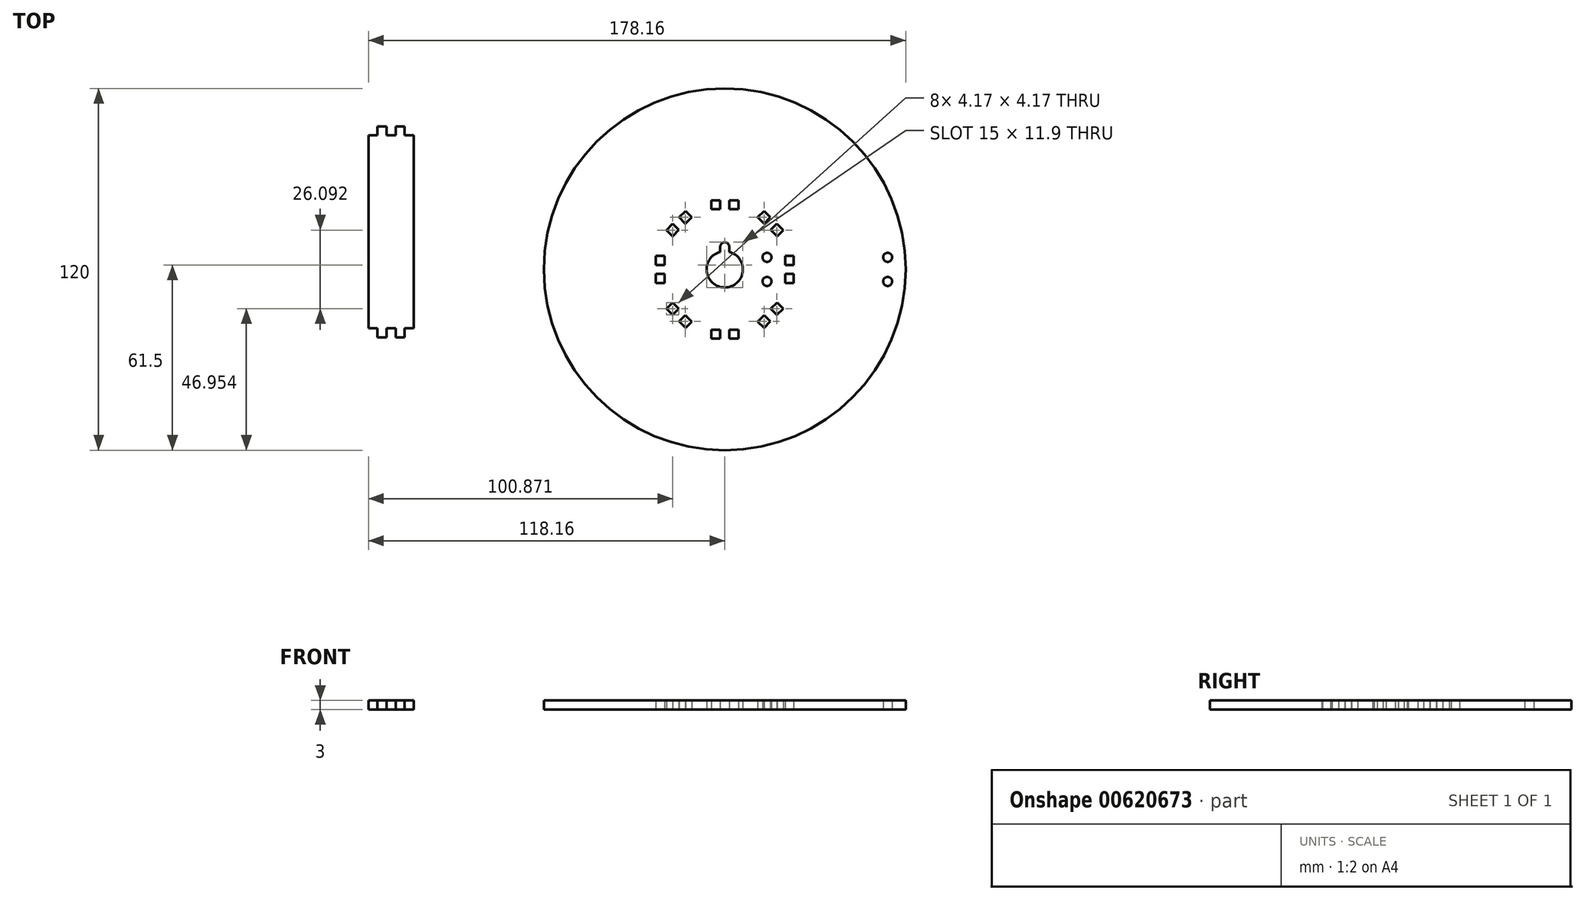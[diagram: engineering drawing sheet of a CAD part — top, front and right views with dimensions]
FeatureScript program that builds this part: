
annotation { "Feature Type Name" : "Feature", "Feature Type Description" : "" }
export const myFeature = defineFeature(function(context is Context, id is Id, definition is map)
    precondition{}
    {
        {
            var Q0;
            Q0=qCreatedBy(makeId("Top.planeOp"),FACE);
            var sketch = newSketch(context, id + "F0", { "sketchPlane" : qUnion([Q0])});
            skCircle(sketch, "E0", {"center": v(0, 0) * mm, "radius": 60 * mm});
            skArc(sketch, "E1", {"start": v(-1.5, 5.8) * mm, "mid": v(0, -6) * mm, "end": v(1.5, 5.8) * mm});
            skCircle(sketch, "E2", {"center": v(0, 0) * mm, "radius": 20 * mm});
            skLineSegment(sketch, "E3.bottom", {"start": v(-286.24, 2.98) * mm, "end": v(-283.34, 2.98) * mm});
            skLineSegment(sketch, "E3.top", {"start": v(-286.24, -0.02) * mm, "end": v(-283.34, -0.02) * mm});
            skLineSegment(sketch, "E3.left", {"start": v(-286.24, 2.98) * mm, "end": v(-286.24, -0.02) * mm});
            skLineSegment(sketch, "E3.right", {"start": v(-283.34, 2.98) * mm, "end": v(-283.34, -0.02) * mm});
            skLineSegment(sketch, "E4.bottom", {"start": v(-286.24, -3.02) * mm, "end": v(-283.34, -3.02) * mm});
            skLineSegment(sketch, "E4.top", {"start": v(-286.24, -6.02) * mm, "end": v(-283.34, -6.02) * mm});
            skLineSegment(sketch, "E4.left", {"start": v(-286.24, -3.02) * mm, "end": v(-286.24, -6.02) * mm});
            skLineSegment(sketch, "E4.right", {"start": v(-283.34, -3.02) * mm, "end": v(-283.34, -6.02) * mm});
            skLineSegment(sketch, "E5.bottom", {"start": v(-243.34, 2.98) * mm, "end": v(-240.44, 2.98) * mm});
            skLineSegment(sketch, "E5.top", {"start": v(-243.34, -0.02) * mm, "end": v(-240.44, -0.02) * mm});
            skLineSegment(sketch, "E5.left", {"start": v(-243.34, 2.98) * mm, "end": v(-243.34, -0.02) * mm});
            skLineSegment(sketch, "E5.right", {"start": v(-240.44, 2.98) * mm, "end": v(-240.44, -0.02) * mm});
            skLineSegment(sketch, "E6.bottom", {"start": v(-243.34, -3.02) * mm, "end": v(-240.44, -3.02) * mm});
            skLineSegment(sketch, "E6.top", {"start": v(-243.34, -6.02) * mm, "end": v(-240.44, -6.02) * mm});
            skLineSegment(sketch, "E6.left", {"start": v(-243.34, -3.02) * mm, "end": v(-243.34, -6.02) * mm});
            skLineSegment(sketch, "E6.right", {"start": v(-240.44, -3.02) * mm, "end": v(-240.44, -6.02) * mm});
            skLineSegment(sketch, "E7.bottom", {"start": v(-258.84, 21.38) * mm, "end": v(-258.84, 18.48) * mm});
            skLineSegment(sketch, "E7.top", {"start": v(-261.84, 21.38) * mm, "end": v(-261.84, 18.48) * mm});
            skLineSegment(sketch, "E7.left", {"start": v(-258.84, 21.38) * mm, "end": v(-261.84, 21.38) * mm});
            skLineSegment(sketch, "E7.right", {"start": v(-258.84, 18.48) * mm, "end": v(-261.84, 18.48) * mm});
            skLineSegment(sketch, "E8.bottom", {"start": v(-264.84, 21.38) * mm, "end": v(-264.84, 18.48) * mm});
            skLineSegment(sketch, "E8.top", {"start": v(-267.84, 21.38) * mm, "end": v(-267.84, 18.48) * mm});
            skLineSegment(sketch, "E8.left", {"start": v(-264.84, 21.38) * mm, "end": v(-267.84, 21.38) * mm});
            skLineSegment(sketch, "E8.right", {"start": v(-264.84, 18.48) * mm, "end": v(-267.84, 18.48) * mm});
            skLineSegment(sketch, "E9.bottom", {"start": v(-258.84, -21.52) * mm, "end": v(-258.84, -24.42) * mm});
            skLineSegment(sketch, "E9.top", {"start": v(-261.84, -21.52) * mm, "end": v(-261.84, -24.42) * mm});
            skLineSegment(sketch, "E9.left", {"start": v(-258.84, -21.52) * mm, "end": v(-261.84, -21.52) * mm});
            skLineSegment(sketch, "E9.right", {"start": v(-258.84, -24.42) * mm, "end": v(-261.84, -24.42) * mm});
            skLineSegment(sketch, "E10.bottom", {"start": v(-264.84, -21.52) * mm, "end": v(-264.84, -24.42) * mm});
            skLineSegment(sketch, "E10.top", {"start": v(-267.84, -21.52) * mm, "end": v(-267.84, -24.42) * mm});
            skLineSegment(sketch, "E10.left", {"start": v(-264.84, -21.52) * mm, "end": v(-267.84, -21.52) * mm});
            skLineSegment(sketch, "E10.right", {"start": v(-264.84, -24.42) * mm, "end": v(-267.84, -24.42) * mm});
            skPoint(sketch, "E11", {"position": v(-263.34, 18.48) * mm});
            skPoint(sketch, "E12", {"position": v(-263.34, -21.52) * mm});
            skPoint(sketch, "E13", {"position": v(-283.34, -1.52) * mm});
            skPoint(sketch, "E14", {"position": v(-243.34, -1.52) * mm});
            skPoint(sketch, "E15", {"position": v(-263.34, -1.52) * mm});
            skLineSegment(sketch, "E16.bottom", {"start": v(-282.72, -14.53) * mm, "end": v(-280.67, -12.48) * mm});
            skLineSegment(sketch, "E16.top", {"start": v(-280.6, -16.65) * mm, "end": v(-278.54, -14.6) * mm});
            skLineSegment(sketch, "E16.left", {"start": v(-282.72, -14.53) * mm, "end": v(-280.6, -16.65) * mm});
            skLineSegment(sketch, "E16.right", {"start": v(-280.67, -12.48) * mm, "end": v(-278.54, -14.6) * mm});
            skLineSegment(sketch, "E17.bottom", {"start": v(-278.47, -18.77) * mm, "end": v(-276.42, -16.72) * mm});
            skLineSegment(sketch, "E17.top", {"start": v(-276.35, -20.9) * mm, "end": v(-274.3, -18.84) * mm});
            skLineSegment(sketch, "E17.left", {"start": v(-278.47, -18.77) * mm, "end": v(-276.35, -20.9) * mm});
            skLineSegment(sketch, "E17.right", {"start": v(-276.42, -16.72) * mm, "end": v(-274.3, -18.84) * mm});
            skLineSegment(sketch, "E18.bottom", {"start": v(-252.38, 15.8) * mm, "end": v(-250.33, 17.85) * mm});
            skLineSegment(sketch, "E18.top", {"start": v(-250.26, 13.68) * mm, "end": v(-248.2, 15.73) * mm});
            skLineSegment(sketch, "E18.left", {"start": v(-252.38, 15.8) * mm, "end": v(-250.26, 13.68) * mm});
            skLineSegment(sketch, "E18.right", {"start": v(-250.33, 17.85) * mm, "end": v(-248.2, 15.73) * mm});
            skLineSegment(sketch, "E19.bottom", {"start": v(-248.14, 11.56) * mm, "end": v(-246.09, 13.61) * mm});
            skLineSegment(sketch, "E19.top", {"start": v(-246.02, 9.44) * mm, "end": v(-243.97, 11.5) * mm});
            skLineSegment(sketch, "E19.left", {"start": v(-248.14, 11.56) * mm, "end": v(-246.02, 9.44) * mm});
            skLineSegment(sketch, "E19.right", {"start": v(-246.09, 13.61) * mm, "end": v(-243.97, 11.5) * mm});
            skLineSegment(sketch, "E20.bottom", {"start": v(-276.35, 17.85) * mm, "end": v(-274.3, 15.8) * mm});
            skLineSegment(sketch, "E20.top", {"start": v(-278.47, 15.73) * mm, "end": v(-276.42, 13.68) * mm});
            skLineSegment(sketch, "E20.left", {"start": v(-276.35, 17.85) * mm, "end": v(-278.47, 15.73) * mm});
            skLineSegment(sketch, "E20.right", {"start": v(-274.3, 15.8) * mm, "end": v(-276.42, 13.68) * mm});
            skLineSegment(sketch, "E21.bottom", {"start": v(-280.6, 13.61) * mm, "end": v(-278.54, 11.56) * mm});
            skLineSegment(sketch, "E21.top", {"start": v(-282.72, 11.5) * mm, "end": v(-280.67, 9.44) * mm});
            skLineSegment(sketch, "E21.left", {"start": v(-280.6, 13.61) * mm, "end": v(-282.72, 11.5) * mm});
            skLineSegment(sketch, "E21.right", {"start": v(-278.54, 11.56) * mm, "end": v(-280.67, 9.44) * mm});
            skLineSegment(sketch, "E22.bottom", {"start": v(-246.02, -12.48) * mm, "end": v(-243.97, -14.53) * mm});
            skLineSegment(sketch, "E22.top", {"start": v(-248.14, -14.6) * mm, "end": v(-246.09, -16.65) * mm});
            skLineSegment(sketch, "E22.left", {"start": v(-246.02, -12.48) * mm, "end": v(-248.14, -14.6) * mm});
            skLineSegment(sketch, "E22.right", {"start": v(-243.97, -14.53) * mm, "end": v(-246.09, -16.65) * mm});
            skLineSegment(sketch, "E23.bottom", {"start": v(-250.26, -16.72) * mm, "end": v(-248.2, -18.77) * mm});
            skLineSegment(sketch, "E23.top", {"start": v(-252.38, -18.84) * mm, "end": v(-250.33, -20.9) * mm});
            skLineSegment(sketch, "E23.left", {"start": v(-250.26, -16.72) * mm, "end": v(-252.38, -18.84) * mm});
            skLineSegment(sketch, "E23.right", {"start": v(-248.2, -18.77) * mm, "end": v(-250.33, -20.9) * mm});
            skPoint(sketch, "E24", {"position": v(-277.48, 12.62) * mm});
            skPoint(sketch, "E25", {"position": v(-249.2, -15.66) * mm});
            skPoint(sketch, "E26", {"position": v(-277.48, -15.66) * mm});
            skPoint(sketch, "E27", {"position": v(-249.2, 12.62) * mm});
            skLineSegment(sketch, "E28.0", {"start": v(-277.48, 12.62) * mm, "end": v(-276.42, 13.68) * mm, "construction": true});
            skLineSegment(sketch, "E28.1", {"start": v(-277.48, 12.62) * mm, "end": v(-277.48, 12.62) * mm});
            skLineSegment(sketch, "E28.8", {"start": v(-277.48, -15.66) * mm, "end": v(-277.48, -15.66) * mm});
            skLineSegment(sketch, "E28.9", {"start": v(-277.48, -15.66) * mm, "end": v(-278.54, -14.6) * mm, "construction": true});
            skLineSegment(sketch, "E28.16", {"start": v(-248.14, 11.56) * mm, "end": v(-248.14, 11.56) * mm});
            skLineSegment(sketch, "E28.17", {"start": v(-248.14, 11.56) * mm, "end": v(-249.2, 12.62) * mm, "construction": true});
            skLineSegment(sketch, "E28.24", {"start": v(-249.2, -15.66) * mm, "end": v(-248.14, -14.6) * mm, "construction": true});
            skLineSegment(sketch, "E28.25", {"start": v(-249.2, -15.66) * mm, "end": v(-249.2, -15.66) * mm});
            skLineSegment(sketch, "E28.32", {"start": v(-249.2, -15.66) * mm, "end": v(-235.06, -1.52) * mm, "construction": true});
            skLineSegment(sketch, "E28.33", {"start": v(-235.06, -1.52) * mm, "end": v(-249.2, 12.62) * mm, "construction": true});
            skLineSegment(sketch, "E28.40", {"start": v(-263.34, -1.52) * mm, "end": v(-249.2, 12.62) * mm, "construction": true});
            skLineSegment(sketch, "E28.41", {"start": v(-263.34, -1.52) * mm, "end": v(-277.48, 12.62) * mm, "construction": true});
            skLineSegment(sketch, "E29.0", {"start": v(-278.54, 11.56) * mm, "end": v(-276.42, 13.68) * mm, "construction": true});
            skLineSegment(sketch, "E30.0", {"start": v(-248.2, -18.77) * mm, "end": v(-246.09, -16.65) * mm, "construction": true});
            skLineSegment(sketch, "E31.0", {"start": v(-280.67, -12.48) * mm, "end": v(-252.38, 15.8) * mm, "construction": true});
            skLineSegment(sketch, "E32.0", {"start": v(-249.2, 12.62) * mm, "end": v(-250.26, 13.68) * mm, "construction": true});
            skLineSegment(sketch, "E33.0", {"start": v(-246.09, 13.61) * mm, "end": v(-248.2, 15.73) * mm, "construction": true});
            skLineSegment(sketch, "E34.0", {"start": v(-276.42, -16.72) * mm, "end": v(-278.54, -14.6) * mm, "construction": true});
            skLineSegment(sketch, "E35.0", {"start": v(-246.02, -12.48) * mm, "end": v(-274.3, 15.8) * mm, "construction": true});
            skLineSegment(sketch, "E36.bottom", {"start": v(-22.9, 4.5) * mm, "end": v(-20, 4.5) * mm});
            skLineSegment(sketch, "E36.top", {"start": v(-22.9, 1.5) * mm, "end": v(-20, 1.5) * mm});
            skLineSegment(sketch, "E36.left", {"start": v(-22.9, 4.5) * mm, "end": v(-22.9, 1.5) * mm});
            skLineSegment(sketch, "E36.right", {"start": v(-20, 4.5) * mm, "end": v(-20, 1.5) * mm});
            skLineSegment(sketch, "E37.bottom", {"start": v(-22.9, -1.5) * mm, "end": v(-20, -1.5) * mm});
            skLineSegment(sketch, "E37.top", {"start": v(-22.9, -4.5) * mm, "end": v(-20, -4.5) * mm});
            skLineSegment(sketch, "E37.left", {"start": v(-22.9, -1.5) * mm, "end": v(-22.9, -4.5) * mm});
            skLineSegment(sketch, "E37.right", {"start": v(-20, -1.5) * mm, "end": v(-20, -4.5) * mm});
            skLineSegment(sketch, "E38.bottom", {"start": v(20, 4.5) * mm, "end": v(22.9, 4.5) * mm});
            skLineSegment(sketch, "E38.top", {"start": v(20, 1.5) * mm, "end": v(22.9, 1.5) * mm});
            skLineSegment(sketch, "E38.left", {"start": v(20, 4.5) * mm, "end": v(20, 1.5) * mm});
            skLineSegment(sketch, "E38.right", {"start": v(22.9, 4.5) * mm, "end": v(22.9, 1.5) * mm});
            skLineSegment(sketch, "E39.bottom", {"start": v(20, -1.5) * mm, "end": v(22.9, -1.5) * mm});
            skLineSegment(sketch, "E39.top", {"start": v(20, -4.5) * mm, "end": v(22.9, -4.5) * mm});
            skLineSegment(sketch, "E39.left", {"start": v(20, -1.5) * mm, "end": v(20, -4.5) * mm});
            skLineSegment(sketch, "E39.right", {"start": v(22.9, -1.5) * mm, "end": v(22.9, -4.5) * mm});
            skLineSegment(sketch, "E40.bottom", {"start": v(4.5, 22.9) * mm, "end": v(4.5, 20) * mm});
            skLineSegment(sketch, "E40.top", {"start": v(1.5, 22.9) * mm, "end": v(1.5, 20) * mm});
            skLineSegment(sketch, "E40.left", {"start": v(4.5, 22.9) * mm, "end": v(1.5, 22.9) * mm});
            skLineSegment(sketch, "E40.right", {"start": v(4.5, 20) * mm, "end": v(1.5, 20) * mm});
            skLineSegment(sketch, "E41.bottom", {"start": v(-1.5, 22.9) * mm, "end": v(-1.5, 20) * mm});
            skLineSegment(sketch, "E41.top", {"start": v(-4.5, 22.9) * mm, "end": v(-4.5, 20) * mm});
            skLineSegment(sketch, "E41.left", {"start": v(-1.5, 22.9) * mm, "end": v(-4.5, 22.9) * mm});
            skLineSegment(sketch, "E41.right", {"start": v(-1.5, 20) * mm, "end": v(-4.5, 20) * mm});
            skLineSegment(sketch, "E42.bottom", {"start": v(4.5, -20) * mm, "end": v(4.5, -22.9) * mm});
            skLineSegment(sketch, "E42.top", {"start": v(1.5, -20) * mm, "end": v(1.5, -22.9) * mm});
            skLineSegment(sketch, "E42.left", {"start": v(4.5, -20) * mm, "end": v(1.5, -20) * mm});
            skLineSegment(sketch, "E42.right", {"start": v(4.5, -22.9) * mm, "end": v(1.5, -22.9) * mm});
            skLineSegment(sketch, "E43.bottom", {"start": v(-1.5, -20) * mm, "end": v(-1.5, -22.9) * mm});
            skLineSegment(sketch, "E43.top", {"start": v(-4.5, -20) * mm, "end": v(-4.5, -22.9) * mm});
            skLineSegment(sketch, "E43.left", {"start": v(-1.5, -20) * mm, "end": v(-4.5, -20) * mm});
            skLineSegment(sketch, "E43.right", {"start": v(-1.5, -22.9) * mm, "end": v(-4.5, -22.9) * mm});
            skPoint(sketch, "E44", {"position": v(0, 20) * mm});
            skPoint(sketch, "E45", {"position": v(0, -20) * mm});
            skPoint(sketch, "E46", {"position": v(-20, 0) * mm});
            skPoint(sketch, "E47", {"position": v(20, 0) * mm});
            skLineSegment(sketch, "E48.bottom", {"start": v(-19.37, -13.01) * mm, "end": v(-17.32, -10.96) * mm});
            skLineSegment(sketch, "E48.top", {"start": v(-17.25, -15.13) * mm, "end": v(-15.2, -13.08) * mm});
            skLineSegment(sketch, "E48.left", {"start": v(-19.37, -13.01) * mm, "end": v(-17.25, -15.13) * mm});
            skLineSegment(sketch, "E48.right", {"start": v(-17.32, -10.96) * mm, "end": v(-15.2, -13.08) * mm});
            skLineSegment(sketch, "E49.bottom", {"start": v(-15.13, -17.25) * mm, "end": v(-13.08, -15.2) * mm});
            skLineSegment(sketch, "E49.top", {"start": v(-13.01, -19.37) * mm, "end": v(-10.96, -17.32) * mm});
            skLineSegment(sketch, "E49.left", {"start": v(-15.13, -17.25) * mm, "end": v(-13.01, -19.37) * mm});
            skLineSegment(sketch, "E49.right", {"start": v(-13.08, -15.2) * mm, "end": v(-10.96, -17.32) * mm});
            skLineSegment(sketch, "E50.bottom", {"start": v(10.96, 17.32) * mm, "end": v(13.01, 19.37) * mm});
            skLineSegment(sketch, "E50.top", {"start": v(13.08, 15.2) * mm, "end": v(15.13, 17.25) * mm});
            skLineSegment(sketch, "E50.left", {"start": v(10.96, 17.32) * mm, "end": v(13.08, 15.2) * mm});
            skLineSegment(sketch, "E50.right", {"start": v(13.01, 19.37) * mm, "end": v(15.13, 17.25) * mm});
            skLineSegment(sketch, "E51.bottom", {"start": v(15.2, 13.08) * mm, "end": v(17.25, 15.13) * mm});
            skLineSegment(sketch, "E51.top", {"start": v(17.32, 10.96) * mm, "end": v(19.37, 13.01) * mm});
            skLineSegment(sketch, "E51.left", {"start": v(15.2, 13.08) * mm, "end": v(17.32, 10.96) * mm});
            skLineSegment(sketch, "E51.right", {"start": v(17.25, 15.13) * mm, "end": v(19.37, 13.01) * mm});
            skLineSegment(sketch, "E52.bottom", {"start": v(-13.01, 19.37) * mm, "end": v(-10.96, 17.32) * mm});
            skLineSegment(sketch, "E52.top", {"start": v(-15.13, 17.25) * mm, "end": v(-13.08, 15.2) * mm});
            skLineSegment(sketch, "E52.left", {"start": v(-13.01, 19.37) * mm, "end": v(-15.13, 17.25) * mm});
            skLineSegment(sketch, "E52.right", {"start": v(-10.96, 17.32) * mm, "end": v(-13.08, 15.2) * mm});
            skLineSegment(sketch, "E53.bottom", {"start": v(-17.25, 15.13) * mm, "end": v(-15.2, 13.08) * mm});
            skLineSegment(sketch, "E53.top", {"start": v(-19.37, 13.01) * mm, "end": v(-17.32, 10.96) * mm});
            skLineSegment(sketch, "E53.left", {"start": v(-17.25, 15.13) * mm, "end": v(-19.37, 13.01) * mm});
            skLineSegment(sketch, "E53.right", {"start": v(-15.2, 13.08) * mm, "end": v(-17.32, 10.96) * mm});
            skLineSegment(sketch, "E54.bottom", {"start": v(17.32, -10.96) * mm, "end": v(19.37, -13.01) * mm});
            skLineSegment(sketch, "E54.top", {"start": v(15.2, -13.08) * mm, "end": v(17.25, -15.13) * mm});
            skLineSegment(sketch, "E54.left", {"start": v(17.32, -10.96) * mm, "end": v(15.2, -13.08) * mm});
            skLineSegment(sketch, "E54.right", {"start": v(19.37, -13.01) * mm, "end": v(17.25, -15.13) * mm});
            skLineSegment(sketch, "E55.bottom", {"start": v(13.08, -15.2) * mm, "end": v(15.13, -17.25) * mm});
            skLineSegment(sketch, "E55.top", {"start": v(10.96, -17.32) * mm, "end": v(13.01, -19.37) * mm});
            skLineSegment(sketch, "E55.left", {"start": v(13.08, -15.2) * mm, "end": v(10.96, -17.32) * mm});
            skLineSegment(sketch, "E55.right", {"start": v(15.13, -17.25) * mm, "end": v(13.01, -19.37) * mm});
            skPoint(sketch, "E56", {"position": v(-14.14, 14.14) * mm});
            skPoint(sketch, "E57", {"position": v(14.14, -14.14) * mm});
            skPoint(sketch, "E58", {"position": v(-14.14, -14.14) * mm});
            skPoint(sketch, "E59", {"position": v(14.14, 14.14) * mm});
            skLineSegment(sketch, "E60.0", {"start": v(-14.14, 14.14) * mm, "end": v(-13.08, 15.2) * mm, "construction": true});
            skLineSegment(sketch, "E60.1", {"start": v(-14.14, 14.14) * mm, "end": v(-14.14, 14.14) * mm});
            skLineSegment(sketch, "E60.8", {"start": v(-14.14, -14.14) * mm, "end": v(-14.14, -14.14) * mm});
            skLineSegment(sketch, "E60.9", {"start": v(-14.14, -14.14) * mm, "end": v(-15.2, -13.08) * mm, "construction": true});
            skLineSegment(sketch, "E60.16", {"start": v(15.2, 13.08) * mm, "end": v(15.2, 13.08) * mm});
            skLineSegment(sketch, "E60.17", {"start": v(15.2, 13.08) * mm, "end": v(14.14, 14.14) * mm, "construction": true});
            skLineSegment(sketch, "E60.24", {"start": v(14.14, -14.14) * mm, "end": v(15.2, -13.08) * mm, "construction": true});
            skLineSegment(sketch, "E60.25", {"start": v(14.14, -14.14) * mm, "end": v(14.14, -14.14) * mm});
            skLineSegment(sketch, "E60.32", {"start": v(14.14, -14.14) * mm, "end": v(28.28, 0) * mm, "construction": true});
            skLineSegment(sketch, "E60.33", {"start": v(28.28, 0) * mm, "end": v(14.14, 14.14) * mm, "construction": true});
            skLineSegment(sketch, "E60.40", {"start": v(0, 0) * mm, "end": v(14.14, 14.14) * mm, "construction": true});
            skLineSegment(sketch, "E60.41", {"start": v(0, 0) * mm, "end": v(-14.14, 14.14) * mm, "construction": true});
            skLineSegment(sketch, "E61.0", {"start": v(-15.2, 13.08) * mm, "end": v(-13.08, 15.2) * mm, "construction": true});
            skLineSegment(sketch, "E62.0", {"start": v(15.13, -17.25) * mm, "end": v(17.25, -15.13) * mm, "construction": true});
            skLineSegment(sketch, "E63.0", {"start": v(-17.32, -10.96) * mm, "end": v(10.96, 17.32) * mm, "construction": true});
            skLineSegment(sketch, "E64.0", {"start": v(14.14, 14.14) * mm, "end": v(13.08, 15.2) * mm, "construction": true});
            skLineSegment(sketch, "E65.0", {"start": v(17.25, 15.13) * mm, "end": v(15.13, 17.25) * mm, "construction": true});
            skLineSegment(sketch, "E66.0", {"start": v(-13.08, -15.2) * mm, "end": v(-15.2, -13.08) * mm, "construction": true});
            skLineSegment(sketch, "E67.0", {"start": v(17.32, -10.96) * mm, "end": v(-10.96, 17.32) * mm, "construction": true});
            skCircle(sketch, "E68", {"center": v(54, 4) * mm, "radius": 1.5 * mm});
            skCircle(sketch, "E69", {"center": v(54, -4) * mm, "radius": 1.5 * mm});
            skCircle(sketch, "E70", {"center": v(14, 4) * mm, "radius": 1.5 * mm});
            skCircle(sketch, "E71", {"center": v(14, -4) * mm, "radius": 1.5 * mm});
            skLineSegment(sketch, "E72.bottom", {"start": v(0, 9) * mm, "end": v(0, 9) * mm});
            skLineSegment(sketch, "E72.top", {"start": v(-1.5, 0) * mm, "end": v(1.5, 0) * mm});
            skLineSegment(sketch, "E72.left", {"start": v(-1.5, 7.5) * mm, "end": v(-1.5, 5.8) * mm});
            skLineSegment(sketch, "E72.right", {"start": v(1.5, 7.5) * mm, "end": v(1.5, 5.8) * mm});
            skPoint(sketch, "E73.visualSharp", {"position": v(-1.5, 9) * mm});
            skArc(sketch, "E73.filletArc", {"start": v(0, 9) * mm, "mid": v(-1.06, 8.56) * mm, "end": v(-1.5, 7.5) * mm});
            skPoint(sketch, "E74.visualSharp", {"position": v(1.5, 9) * mm});
            skArc(sketch, "E74.filletArc", {"start": v(1.5, 7.5) * mm, "mid": v(1.06, 8.56) * mm, "end": v(0, 9) * mm});
            skLineSegment(sketch, "E75.trimOffspring", {"start": v(-1.5, 4.86) * mm, "end": v(-1.5, 0) * mm});
            skLineSegment(sketch, "E76.trimOffspring", {"start": v(1.5, 4.86) * mm, "end": v(1.5, 0) * mm});
            skSolve(sketch);
        }
        {
            var Q0;
            Q0=qCreatedBy(makeId("Top.planeOp"),FACE);
            var sketch = newSketch(context, id + "F1", { "sketchPlane" : qUnion([Q0])});
            skLineSegment(sketch, "E77.bottom", {"start": v(-115.16, 47.44) * mm, "end": v(-112.16, 47.44) * mm});
            skLineSegment(sketch, "E77.top", {"start": v(-115.16, -22.56) * mm, "end": v(-112.16, -22.56) * mm});
            skLineSegment(sketch, "E77.left", {"start": v(-115.16, 47.44) * mm, "end": v(-115.16, 44.44) * mm});
            skLineSegment(sketch, "E77.right", {"start": v(-106.16, 47.44) * mm, "end": v(-106.16, 44.44) * mm});
            skLineSegment(sketch, "E78.top", {"start": v(-112.16, 44.44) * mm, "end": v(-109.16, 44.44) * mm});
            skLineSegment(sketch, "E78.left", {"start": v(-112.16, 47.44) * mm, "end": v(-112.16, 44.44) * mm});
            skLineSegment(sketch, "E78.right", {"start": v(-109.16, 47.44) * mm, "end": v(-109.16, 44.44) * mm});
            skLineSegment(sketch, "E79.bottom", {"start": v(-112.16, -19.56) * mm, "end": v(-109.16, -19.56) * mm});
            skLineSegment(sketch, "E79.left", {"start": v(-112.16, -19.56) * mm, "end": v(-112.16, -22.56) * mm});
            skLineSegment(sketch, "E79.right", {"start": v(-109.16, -19.56) * mm, "end": v(-109.16, -22.56) * mm});
            skLineSegment(sketch, "E80.trimOffspring", {"start": v(-109.16, 47.44) * mm, "end": v(-106.16, 47.44) * mm});
            skLineSegment(sketch, "E81.trimOffspring", {"start": v(-109.16, -22.56) * mm, "end": v(-106.16, -22.56) * mm});
            skLineSegment(sketch, "E82.bottom", {"start": v(-106.16, 44.44) * mm, "end": v(-103.16, 44.44) * mm});
            skLineSegment(sketch, "E82.top", {"start": v(-106.16, -19.56) * mm, "end": v(-103.16, -19.56) * mm});
            skLineSegment(sketch, "E82.right", {"start": v(-103.16, 44.44) * mm, "end": v(-103.16, -19.56) * mm});
            skLineSegment(sketch, "E83.bottom", {"start": v(-115.16, -19.56) * mm, "end": v(-118.16, -19.56) * mm});
            skLineSegment(sketch, "E83.top", {"start": v(-115.16, 44.44) * mm, "end": v(-118.16, 44.44) * mm});
            skLineSegment(sketch, "E83.right", {"start": v(-118.16, -19.56) * mm, "end": v(-118.16, 44.44) * mm});
            skLineSegment(sketch, "E84.trimOffspring", {"start": v(-106.16, -19.56) * mm, "end": v(-106.16, -22.56) * mm});
            skLineSegment(sketch, "E85.trimOffspring", {"start": v(-115.16, -19.56) * mm, "end": v(-115.16, -22.56) * mm});
            skSolve(sketch);
        }
        {
            var Q0;
            Q0 = qSketchRegion(id + "F1", true);
            extrude(context, id + "F2", {"entities" : qUnion([Q0]), "depth" : 3 * mm, "offsetDistance" : 25 * mm});
        }
        {
            var Q0;
            Q0=makeQuery(id+"F0.imprint","IMPRINT",FACE,{"disambiguationData":[TD([[makeQuery(id+"F0.imprint","IMPRINT",EDGE,{"derivedFrom":sQuery(id+"F0.wireOp",EDGE,"E0")}),1.0]])]});
            var Q1;
            Q1=makeQuery(id+"F0.imprint","IMPRINT",FACE,{"disambiguationData":[TD([[makeQuery(id+"F0.imprint","IMPRINT",EDGE,{"derivedFrom":sQuery(id+"F0.wireOp",EDGE,"E2")}),1.0]])]});
            extrude(context, id + "F3", {"entities" : qUnion([Q0, Q1]), "depth" : 3 * mm, "offsetDistance" : 25 * mm});
        }
    });
